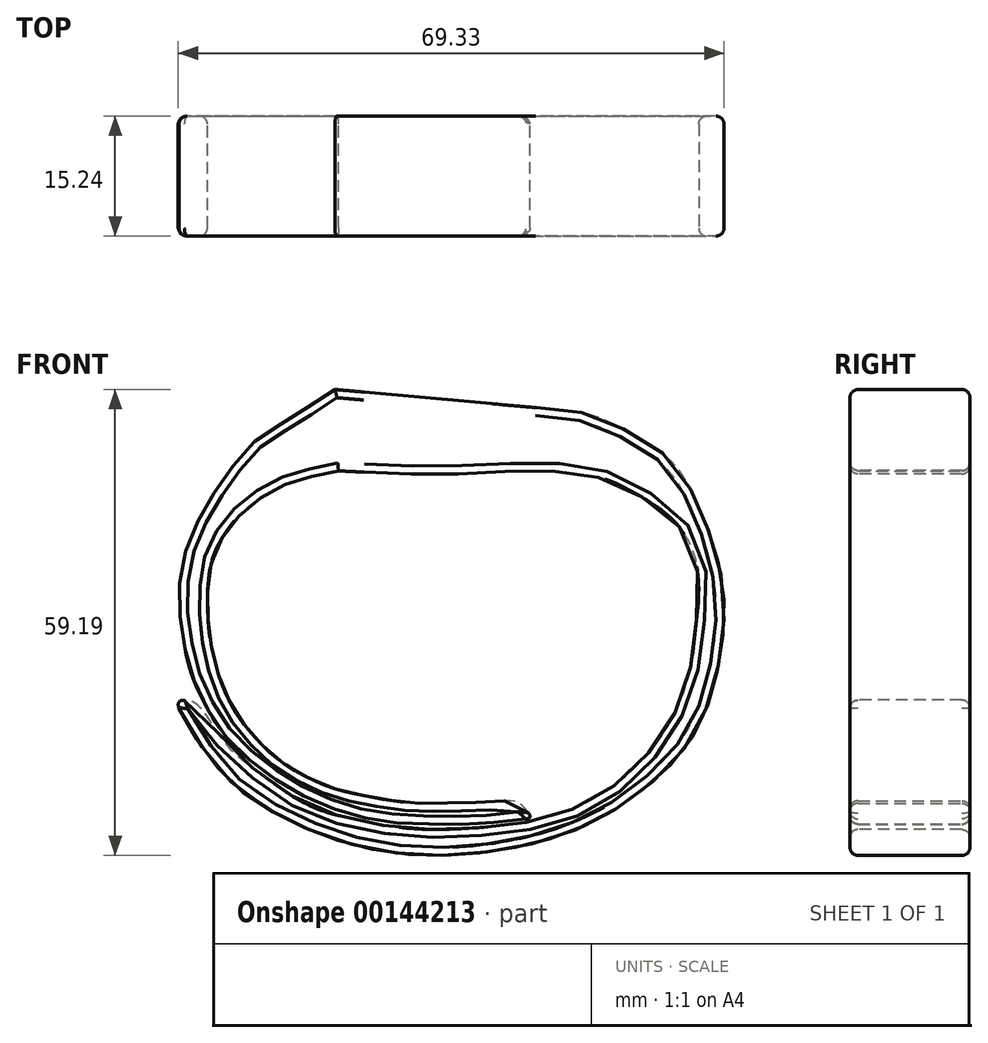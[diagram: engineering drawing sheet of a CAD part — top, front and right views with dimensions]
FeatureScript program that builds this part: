
annotation { "Feature Type Name" : "Feature", "Feature Type Description" : "" }
export const myFeature = defineFeature(function(context is Context, id is Id, definition is map)
    precondition{}
    {
        {
            var Q0;
            Q0=qCreatedBy(makeId("Right.planeOp"),FACE);
            var sketch = newSketch(context, id + "F0", { "sketchPlane" : qUnion([Q0])});
            skLineSegment(sketch, "E0.bottom", {"start": v(21.06, 43.42) * mm, "end": v(-21.06, 43.42) * mm});
            skLineSegment(sketch, "E0.top", {"start": v(21.06, 58.18) * mm, "end": v(-21.06, 58.18) * mm});
            skLineSegment(sketch, "E0.left", {"start": v(21.06, 43.42) * mm, "end": v(21.06, 58.18) * mm});
            skLineSegment(sketch, "E0.right", {"start": v(-21.06, 43.42) * mm, "end": v(-21.06, 58.18) * mm});
            skPoint(sketch, "E0.middle", {"position": v(0, 50.8) * mm});
            skLineSegment(sketch, "E1.bottom", {"start": v(21.06, -48.2) * mm, "end": v(-21.06, -48.2) * mm});
            skLineSegment(sketch, "E1.top", {"start": v(21.06, -43.85) * mm, "end": v(-21.06, -43.85) * mm});
            skLineSegment(sketch, "E1.left", {"start": v(21.06, -48.2) * mm, "end": v(21.06, -43.85) * mm});
            skLineSegment(sketch, "E1.right", {"start": v(-21.06, -48.2) * mm, "end": v(-21.06, -43.85) * mm});
            skPoint(sketch, "E1.middle", {"position": v(0, -46.02) * mm});
            skSolve(sketch);
        }
        {
            var Q0;
            Q0=qCreatedBy(makeId("Front.planeOp"),FACE);
            var sketch = newSketch(context, id + "F1", { "sketchPlane" : qUnion([Q0])});
            skFitSpline(sketch, "E2", {"points": [v(-12.06, 28.74) * mm, v(-6.81, 28.28) * mm, v(3.52, 27.35) * mm, v(13.54, 26.43) * mm, v(20.48, 25.5) * mm, v(24.96, 23.5) * mm, v(30.5, 19.8) * mm, v(34.36, 13.47) * mm, v(37.14, 4.22) * mm, v(36.68, -6.26) * mm, v(32.97, -15.98) * mm, v(25.57, -23.23) * mm, v(18.02, -27.4) * mm, v(7.38, -30.01) * mm, v(-4.04, -30.17) * mm, v(-14.37, -27.55) * mm, v(-23.31, -22.77) * mm, v(-28.4, -17.37) * mm, v(-31.95, -11.2) * mm, v(-31.33, -10.74) * mm, v(-29.64, -11.2) * mm, v(-27.32, -14.28) * mm, v(-24.24, -17.98) * mm, v(-20.54, -20.76) * mm, v(-14.83, -24.3) * mm, v(-3.57, -26.93) * mm, v(3.37, -27.08) * mm, v(13.39, -26) * mm, v(21.4, -22.92) * mm, v(28.2, -16.9) * mm, v(32.51, -8.89) * mm, v(33.75, -1.8) * mm, v(34.05, 5.46) * mm, v(30.97, 12.09) * mm, v(24.5, 16.4) * mm, v(22.33, 17.33) * mm, v(15.09, 18.4) * mm, v(5.68, 18.1) * mm, v(-4.8, 18.1) * mm, v(-11.6, 18.4) * mm], "startDerivative": vector(221.33, -19.58) * mm, "endDerivative": vector(-259.3, 13.94) * mm});
            skLineSegment(sketch, "E3", {"start": v(-8.36, 28.41) * mm, "end": v(-8.36, 18.24) * mm});
            skLineSegment(sketch, "E4", {"start": v(-12.06, 28.74) * mm, "end": v(-11.6, 18.4) * mm});
            skFitSpline(sketch, "E5", {"points": [v(-12.06, 28.74) * mm, v(-17.76, 25.04) * mm, v(-22.08, 22.26) * mm, v(-25.63, 18.1) * mm, v(-28.86, 13.17) * mm, v(-31.64, 5.3) * mm, v(-31.33, -3.03) * mm, v(-29.64, -9.04) * mm, v(-26.3, -14.78) * mm, v(-22.96, -18.25) * mm, v(-18.4, -21.6) * mm, v(-14.83, -23.45) * mm, v(-10.94, -24.95) * mm, v(-6.44, -25.99) * mm, v(-1.82, -26.45) * mm, v(1.3, -26.45) * mm, v(5.92, -26.45) * mm, v(10.95, -25.93) * mm, v(12.74, -25.59) * mm, v(12.4, -24.83) * mm, v(11.18, -23.68) * mm, v(8.93, -23.56) * mm, v(6.04, -23.74) * mm, v(2.05, -23.8) * mm, v(-2.68, -23.74) * mm, v(-7.36, -23.04) * mm, v(-11.29, -22.24) * mm, v(-14, -21.25) * mm, v(-16.95, -19.75) * mm, v(-19.78, -17.84) * mm, v(-22.26, -15.36) * mm, v(-24.7, -12.24) * mm, v(-26.83, -7.56) * mm, v(-28.04, -1.9) * mm, v(-28.21, 3.07) * mm, v(-27.52, 7.46) * mm, v(-25.56, 11.15) * mm, v(-23.19, 13.7) * mm, v(-19.66, 16.06) * mm, v(-16.03, 17.45) * mm, v(-14, 17.85) * mm, v(-11.6, 18.4) * mm], "startDerivative": vector(-188.07, -127.01) * mm, "endDerivative": vector(133.81, 32.95) * mm});
            skLineSegment(sketch, "E6", {"start": v(13.54, 26.43) * mm, "end": v(-8.36, 28.41) * mm});
            skSolve(sketch);
        }
        {
            var Q0;
            {var subQ0=sQuery(id+"F1.wireOp",EDGE,"E6");var subQ1=sQuery(id+"F1.wireOp",EDGE,"E2");var subQ3=makeQuery(id+"F1.imprint","INTERSECT",VERTEX,{"disambiguationData":[OD(1.0)],"derivedFrom":[subQ1,subQ0]});Q0=makeQuery(id+"F1.imprint","IMPRINT",FACE,{"disambiguationData":[TD([[makeQuery(id+"F1.imprint","IMPRINT",EDGE,{"disambiguationData":[TD([[subQ3,1.0]])],"derivedFrom":subQ1}),-1.0]])]});}
            var Q1;
            {var subQ4=sQuery(id+"F1.wireOp",EDGE,"E3");Q1=makeQuery(id+"F1.imprint","IMPRINT",FACE,{"disambiguationData":[TD([[makeQuery(id+"F1.imprint","IMPRINT",EDGE,{"derivedFrom":subQ4}),1.0]])]});}
            var Q2;
            Q2=makeQuery(id+"F1.imprint","IMPRINT",FACE,{"disambiguationData":[TD([[makeQuery(id+"F1.imprint","IMPRINT",EDGE,{"derivedFrom":sQuery(id+"F1.wireOp",EDGE,"E4")}),-1.0]])]});
            var Q3;
            {var subQ3=sQuery(id+"F1.wireOp",EDGE,"E3");Q3=makeQuery(id+"F1.imprint","IMPRINT",FACE,{"disambiguationData":[TD([[makeQuery(id+"F1.imprint","IMPRINT",EDGE,{"derivedFrom":subQ3}),-1.0]])]});}
            extrude(context, id + "F2", {"entities" : qUnion([Q0, Q1, Q2, Q3]), "endBound" : BoundingType.SYMMETRIC, "depth" : 15.24 * mm});
        }
        {
            var Q0;
            Q0=makeQuery(id+"F2.opExtrude","CAP_EDGE",EDGE,{"disambiguationData":[OSD([sQuery(id+"F1.wireOp",EDGE,"E2")])],"isStart":false});
            var Q1;
            Q1=makeQuery(id+"F2.opExtrude","CAP_EDGE",EDGE,{"disambiguationData":[OSD([sQuery(id+"F1.wireOp",EDGE,"E5")])],"isStart":false});
            fillet(context, id + "F3", {"entities" : qUnion([Q0, Q1]), "radius" : 1.02 * mm, "tangentPropagation" : true, "allowEdgeOverflow" : false});
        }
        {
            var Q0;
            Q0=makeQuery(id+"F2.opExtrude","CAP_EDGE",EDGE,{"disambiguationData":[OSD([sQuery(id+"F1.wireOp",EDGE,"E2")])],"isStart":true});
            var Q1;
            Q1=makeQuery(id+"F2.opExtrude","CAP_EDGE",EDGE,{"disambiguationData":[OSD([sQuery(id+"F1.wireOp",EDGE,"E5")])],"isStart":true});
            fillet(context, id + "F4", {"entities" : qUnion([Q0, Q1]), "radius" : 1.02 * mm, "tangentPropagation" : true, "allowEdgeOverflow" : false});
        }
    });
